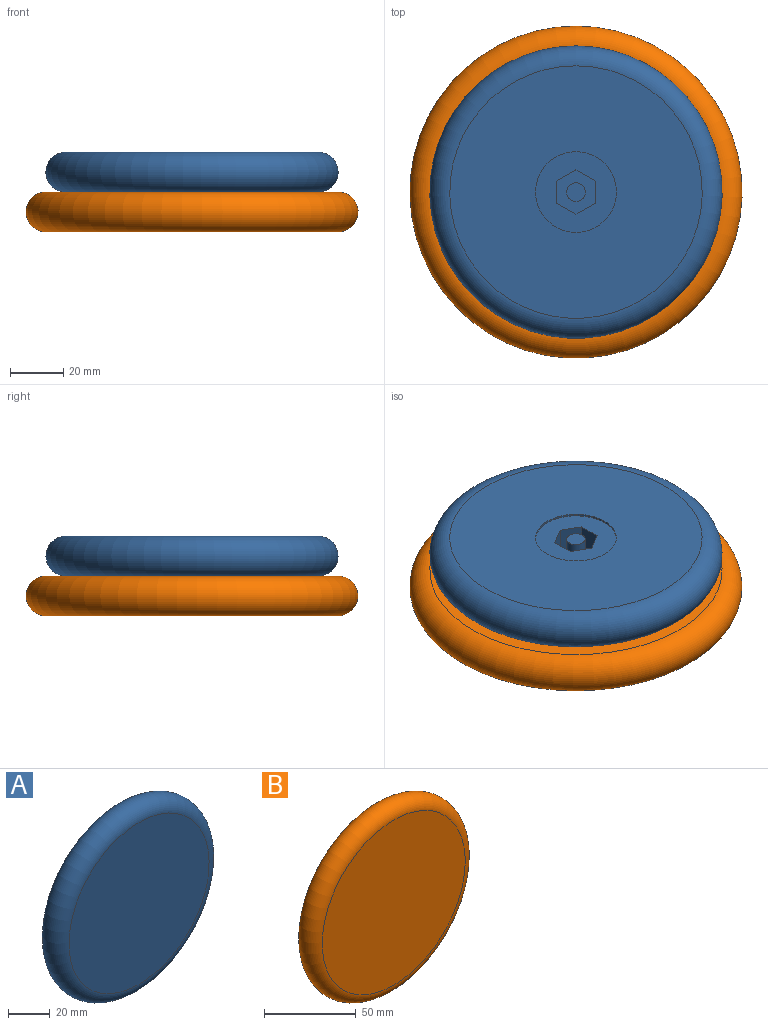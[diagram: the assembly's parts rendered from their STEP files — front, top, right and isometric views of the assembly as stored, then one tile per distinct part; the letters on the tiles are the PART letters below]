
ASSEMBLY  parts=2 mates=1
PART A: 14 faces, bbox 119.1x15x119.1 mm
  f0: plane 30.4x30.4mm, normal (0,1,0), area 546.3mm2, adj f4,f5,f6,f7,f8,f9,f10
  f1: plane 95x95mm, normal (0,-1,0), area 7088.2mm2, adj f3
  f2: plane 95x95mm, normal (0,1,0), area 6362.4mm2, adj f3,f4
  f3: torus R=47.5mm, axis (0,-1,0), area 7739mm2, adj f1,f2
  f4: cylinder r=15.2mm len=30.4mm, axis (0,1,0), area 66.9mm2, adj f0,f2
  f5: plane 10x7.2mm, normal (0.5,0,0.87), area 83.1mm2, adj f0,f6,f10,f12
  f6: plane 10x8.31mm, normal (1,0,0), area 83.1mm2, adj f0,f5,f7,f12
  f7: plane 10x7.2mm, normal (0.5,0,-0.87), area 83.1mm2, adj f0,f6,f8,f12
  f8: plane 10x7.2mm, normal (-0.5,0,-0.87), area 83.1mm2, adj f0,f7,f9,f12
  f9: plane 10x8.31mm, normal (-1,0,0), area 83.1mm2, adj f0,f8,f10,f12
  f10: plane 10x7.2mm, normal (-0.5,0,0.87), area 83.1mm2, adj f0,f5,f9,f12
  f11: cylinder r=3.5mm len=10mm, axis (0,1,0), area 219.9mm2, adj f12,f13
  f12: plane 16.63x14.4mm, normal (0,1,0), area 141.1mm2, adj f5,f6,f7,f8,f9,f10,f11
  f13: plane 7x7mm, normal (0,1,0), area 38.5mm2, adj f11
PART B: 14 faces, bbox 135.3x15x135.3 mm
  f0: plane 30.4x30.4mm, normal (0,1,0), area 546.3mm2, adj f4,f5,f6,f7,f8,f9,f10
  f1: plane 110x110mm, normal (0,-1,0), area 9503.3mm2, adj f3
  f2: plane 110x110mm, normal (0,1,0), area 8777.5mm2, adj f3,f4
  f3: torus R=55mm, axis (0,-1,0), area 8849.3mm2, adj f1,f2
  f4: cylinder r=15.2mm len=30.4mm, axis (0,1,0), area 66.9mm2, adj f0,f2
  f5: plane 10x7.2mm, normal (0.5,0,0.87), area 83.1mm2, adj f0,f6,f10,f12
  f6: plane 10x8.31mm, normal (1,0,0), area 83.1mm2, adj f0,f5,f7,f12
  f7: plane 10x7.2mm, normal (0.5,0,-0.87), area 83.1mm2, adj f0,f6,f8,f12
  f8: plane 10x7.2mm, normal (-0.5,0,-0.87), area 83.1mm2, adj f0,f7,f9,f12
  f9: plane 10x8.31mm, normal (-1,0,0), area 83.1mm2, adj f0,f8,f10,f12
  f10: plane 10x7.2mm, normal (-0.5,0,0.87), area 83.1mm2, adj f0,f5,f9,f12
  f11: cylinder r=3.5mm len=10mm, axis (0,1,0), area 219.9mm2, adj f12,f13
  f12: plane 16.63x14.4mm, normal (0,1,0), area 141.1mm2, adj f5,f6,f7,f8,f9,f10,f11
  f13: plane 7x7mm, normal (0,1,0), area 38.5mm2, adj f11
PLACE A rot(axis=(1,0,0),90deg) t=(0,0,15.7)mm
PLACE B rot(axis=(1,0,0),90deg) t=(0,-135,0.7)mm
MATE fastened B.f4 <-> A.f4  axis (0,0,1) through (0,0,0)mm
